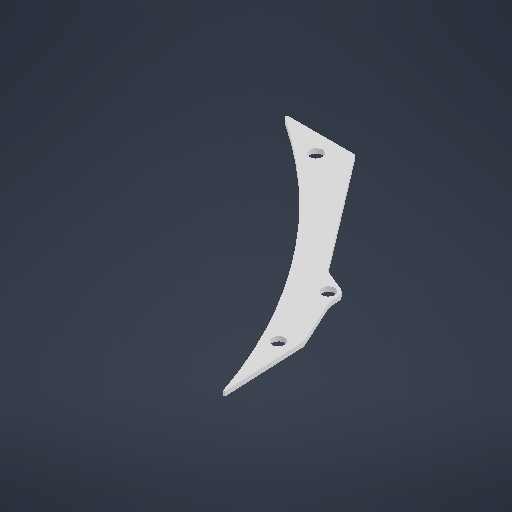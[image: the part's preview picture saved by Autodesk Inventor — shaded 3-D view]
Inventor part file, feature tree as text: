
AUTODESK INVENTOR PART (.ipt)
format: ipt  version: 2025.2 (Build 292293000, 293)  size: 209,408 bytes
history: native  units: in
note: dims shown in document units (in); Inventor stores cm internally (conversion verified against a paired STEP export)
features: extrude x1, sketch x1
ambient origin geometry x8: Origin, YZ Plane, XZ Plane, XY Plane, X Axis, Y Axis, Z Axis, Center Point
bodies: Body1 (feature_tree)
feature tree (2):
  extrude  "Extrusion2"  Depth=0.0625in
  sketch  "Sketch1"  dims[d5=0.172in d9=0.172in d10=0.172in d12=0.025in d26=0.025in d29=0.0625in d30=0.0in]
